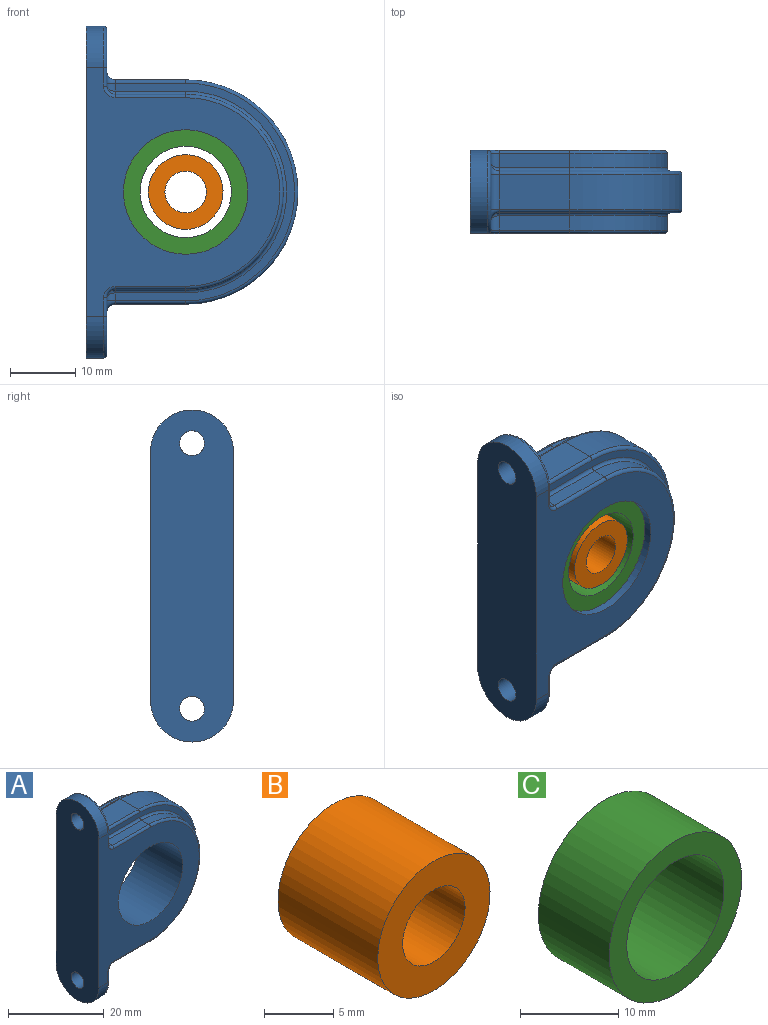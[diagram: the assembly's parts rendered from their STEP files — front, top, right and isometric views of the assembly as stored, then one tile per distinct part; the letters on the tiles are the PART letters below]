
ASSEMBLY  parts=3 mates=2
PART A: 67 faces, bbox 33.8x13.7x51.8 mm
  f0: cylinder r=1.27mm len=5.33mm, axis (0,-1,0), area 10.6mm2, adj f7,f17,f43,f44,f65
  f1: plane 11.69x8.69mm, normal (1,0,0), area 56.9mm2, adj f31,f33,f34,f35,f36,f37,f39,f60
  f2: plane 50.8x12.7mm, normal (-1,0,0), area 587.7mm2, adj f3,f4,f16,f18,f64,f65
  f3: plane 38.1x29.67mm, normal (0,-1,0), area 507.7mm2, adj f2,f16,f18,f48,f50,f52,f54,f56
  f4: plane 38.1x29.67mm, normal (0,1,0), area 507.7mm2, adj f2,f16,f18,f51,f53,f55,f57,f59
  f5: plane 10.8x2.16mm, normal (0,0,1), area 23.3mm2, adj f10,f28,f47,f55
  f6: plane 33.33x27.46mm, normal (0,1,0), area 87.8mm2, adj f25,f26,f27,f28,f29,f30,f37,f45
  f7: plane 10.8x5.33mm, normal (0,0,1), area 57.6mm2, adj f0,f11,f22,f25
  f8: plane 33.33x27.46mm, normal (0,-1,0), area 87.8mm2, adj f19,f20,f21,f22,f23,f24,f33,f42
  f9: plane 10.8x2.16mm, normal (0,0,1), area 23.3mm2, adj f12,f19,f40,f52
  f10: cylinder r=14.94mm len=29.87mm, axis (0,1,0), area 101.3mm2, adj f5,f13,f29,f57
  f11: cylinder r=17.17mm len=34.34mm, axis (0,1,0), area 287.7mm2, adj f7,f14,f23,f26
  f12: cylinder r=14.94mm len=29.87mm, axis (0,1,0), area 101.3mm2, adj f9,f15,f20,f54
  f13: plane 10.8x2.16mm, normal (0,0,-1), area 23.3mm2, adj f10,f30,f39,f59
  f14: plane 10.8x5.33mm, normal (0,0,-1), area 57.6mm2, adj f11,f24,f27,f35
  f15: plane 10.8x2.16mm, normal (0,0,-1), area 23.3mm2, adj f12,f21,f31,f56
  f16: cylinder r=6.35mm len=12.7mm, axis (-1,0,0), area 53.2mm2, adj f2,f3,f4,f49
  f17: plane 11.69x8.69mm, normal (1,0,0), area 56.9mm2, adj f0,f40,f42,f43,f44,f45,f47,f48
  f18: cylinder r=6.35mm len=12.7mm, axis (-1,0,0), area 53.2mm2, adj f2,f3,f4,f62
  f19: cylinder r=0.51mm len=10.8mm, axis (-1,0,0), area 8.6mm2, adj f8,f9,f20,f41
  f20: torus R=15.44mm, axis (0,-1,0), area 37.9mm2, adj f8,f12,f19,f21
  f21: cylinder r=0.51mm len=10.8mm, axis (1,0,0), area 8.6mm2, adj f8,f15,f20,f32
  f22: cylinder r=0.51mm len=10.8mm, axis (1,0,0), area 8.6mm2, adj f7,f8,f23,f43
  f23: torus R=16.66mm, axis (0,-1,0), area 42.6mm2, adj f8,f11,f22,f24
  f24: cylinder r=0.51mm len=10.8mm, axis (-1,0,0), area 8.6mm2, adj f8,f14,f23,f34
  f25: cylinder r=0.51mm len=10.8mm, axis (1,0,0), area 8.6mm2, adj f6,f7,f26,f44
  f26: torus R=16.66mm, axis (0,1,0), area 42.6mm2, adj f6,f11,f25,f27
  f27: cylinder r=0.51mm len=10.8mm, axis (-1,0,0), area 8.6mm2, adj f6,f14,f26,f36
  f28: cylinder r=0.51mm len=10.8mm, axis (-1,0,0), area 8.6mm2, adj f5,f6,f29,f46
  f29: torus R=15.44mm, axis (0,1,0), area 37.9mm2, adj f6,f10,f28,f30
  f30: cylinder r=0.51mm len=10.8mm, axis (1,0,0), area 8.6mm2, adj f6,f13,f29,f38
  f31: cylinder r=1.27mm len=2.16mm, axis (0,1,0), area 3.5mm2, adj f1,f15,f32,f58
  f32: bspline ~1.5x1.27mm, area 0.7mm2, adj f21,f31,f33
  f33: cylinder r=1.27mm len=1.27mm, axis (0,0,-1), area 1.7mm2, adj f1,f8,f32,f34
  f34: torus R=1.78mm, axis (1,0,0), area 3mm2, adj f1,f24,f33,f35
  f35: cylinder r=1.27mm len=5.33mm, axis (0,1,0), area 10.6mm2, adj f1,f14,f34,f36,f64
  f36: torus R=1.78mm, axis (1,0,0), area 3mm2, adj f1,f27,f35,f37
  f37: cylinder r=1.27mm len=1.27mm, axis (0,0,1), area 1.7mm2, adj f1,f6,f36,f38
  f38: bspline ~1.5x1.27mm, area 0.7mm2, adj f30,f37,f39
  f39: cylinder r=1.27mm len=2.16mm, axis (0,1,0), area 3.5mm2, adj f1,f13,f38,f61
  f40: cylinder r=1.27mm len=2.16mm, axis (0,-1,0), area 3.5mm2, adj f9,f17,f41,f50
  f41: bspline ~1.5x1.27mm, area 0.7mm2, adj f19,f40,f42
  f42: cylinder r=1.27mm len=1.27mm, axis (0,0,-1), area 1.7mm2, adj f8,f17,f41,f43
  f43: torus R=1.78mm, axis (1,0,0), area 3mm2, adj f0,f17,f22,f42
  f44: torus R=1.78mm, axis (1,0,0), area 3mm2, adj f0,f17,f25,f45
  f45: cylinder r=1.27mm len=1.27mm, axis (0,0,1), area 1.7mm2, adj f6,f17,f44,f46
  f46: bspline ~1.5x1.27mm, area 0.7mm2, adj f28,f45,f47
  f47: cylinder r=1.27mm len=2.16mm, axis (0,-1,0), area 3.5mm2, adj f5,f17,f46,f53
  f48: cylinder r=0.51mm len=2.85mm, axis (0,0,-1), area 2.3mm2, adj f3,f17,f49,f50
  f49: torus R=5.84mm, axis (1,0,0), area 15.5mm2, adj f16,f17,f48,f51
  f50: torus R=1.78mm, axis (0,-1,0), area 1.8mm2, adj f3,f40,f48,f52
  f51: cylinder r=0.51mm len=2.85mm, axis (0,0,1), area 2.3mm2, adj f4,f17,f49,f53
  f52: cylinder r=0.51mm len=10.8mm, axis (1,0,0), area 8.6mm2, adj f3,f9,f50,f54
  f53: torus R=1.78mm, axis (0,1,0), area 1.8mm2, adj f4,f47,f51,f55
  f54: torus R=14.43mm, axis (0,-1,0), area 37mm2, adj f3,f12,f52,f56
  f55: cylinder r=0.51mm len=10.8mm, axis (1,0,0), area 8.6mm2, adj f4,f5,f53,f57
  f56: cylinder r=0.51mm len=10.8mm, axis (-1,0,0), area 8.6mm2, adj f3,f15,f54,f58
  f57: torus R=14.43mm, axis (0,1,0), area 37mm2, adj f4,f10,f55,f59
  f58: torus R=1.78mm, axis (0,-1,0), area 1.8mm2, adj f3,f31,f56,f60
  f59: cylinder r=0.51mm len=10.8mm, axis (-1,0,0), area 8.6mm2, adj f4,f13,f57,f61
  f60: cylinder r=0.51mm len=2.84mm, axis (0,0,1), area 2.3mm2, adj f1,f3,f58,f62
  f61: torus R=1.78mm, axis (0,1,0), area 1.8mm2, adj f4,f39,f59,f63
  f62: torus R=5.84mm, axis (1,0,0), area 15.5mm2, adj f1,f18,f60,f63
  f63: cylinder r=0.51mm len=2.85mm, axis (0,0,-1), area 2.3mm2, adj f1,f4,f61,f62
  f64: cylinder r=1.91mm len=3.81mm, axis (1,0,0), area 38mm2, adj f1,f2,f35
  f65: cylinder r=1.91mm len=3.81mm, axis (1,0,0), area 38mm2, adj f0,f2,f17
  f66: cylinder r=9.53mm len=19.05mm, axis (0,-1,0), area 760.1mm2, adj f3,f4
PART B: 4 faces, bbox 11.4x10.2x11.4 mm
  f0: plane 11.43x11.43mm, normal (0,-1,0), area 70.9mm2, adj f2,f3
  f1: plane 11.43x11.43mm, normal (0,1,0), area 70.9mm2, adj f2,f3
  f2: cylinder r=3.17mm len=10.16mm, axis (0,1,0), area 202.7mm2, adj f0,f1
  f3: cylinder r=5.71mm len=11.43mm, axis (0,-1,0), area 364.8mm2, adj f0,f1
PART C: 4 faces, bbox 19.1x10.2x19.1 mm
  f0: plane 19.05x19.05mm, normal (0,-1,0), area 131.7mm2, adj f1,f3
  f1: cylinder r=9.53mm len=19.05mm, axis (0,1,0), area 608mm2, adj f0,f2
  f2: plane 19.05x19.05mm, normal (0,1,0), area 131.7mm2, adj f1,f3
  f3: cylinder r=6.99mm len=13.97mm, axis (0,-1,0), area 445.9mm2, adj f0,f2
PLACE A t=(-15.24,0,0)mm
PLACE B at identity
PLACE C at identity
MATE revolute B.f2 <-> A.f66  axis (0,1,0) through (0,0,0)mm
MATE revolute B.f2 <-> C.f3  axis (0,1,0) through (0,0,0)mm
